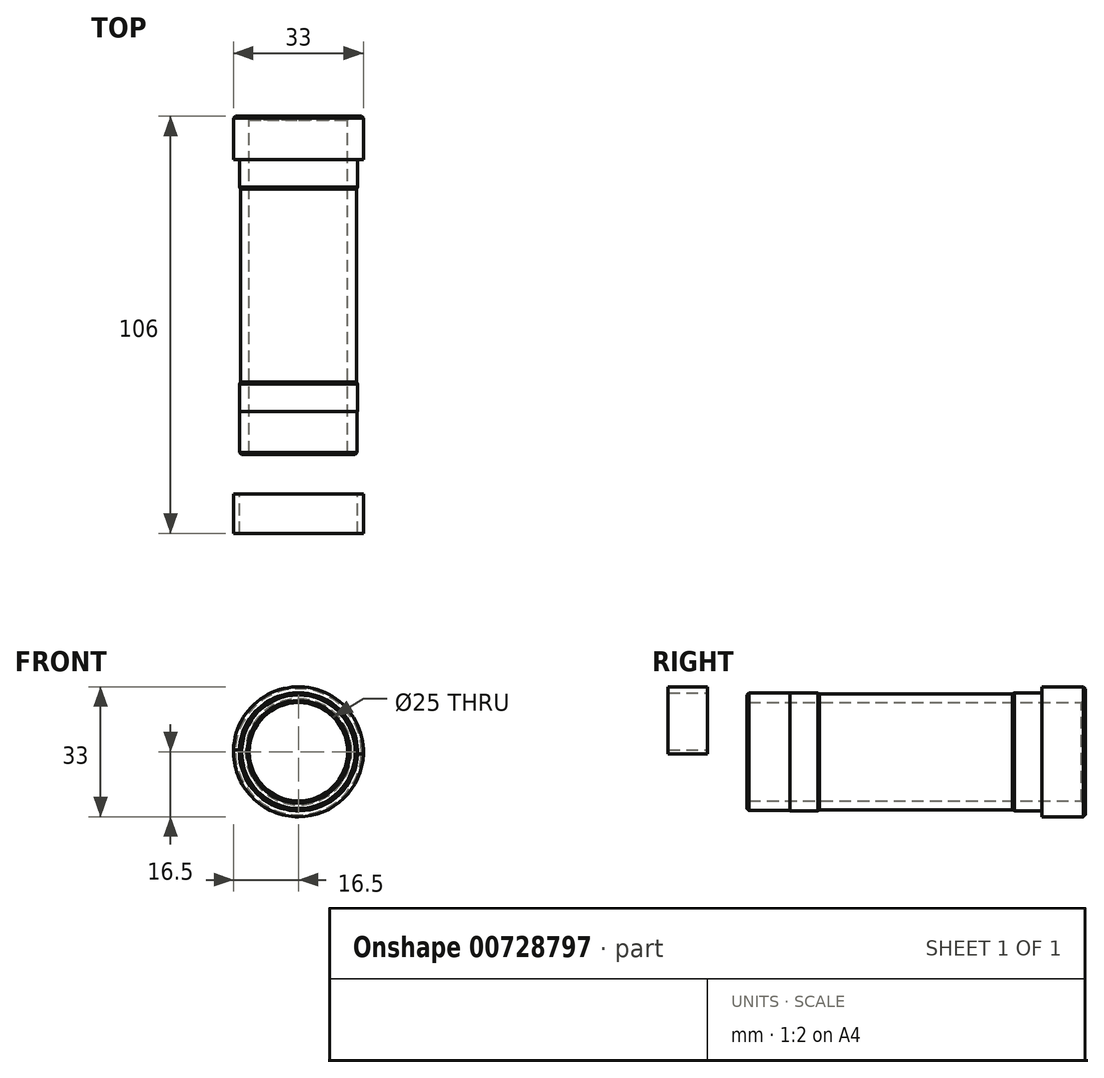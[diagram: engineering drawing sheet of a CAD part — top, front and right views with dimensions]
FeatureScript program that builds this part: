
annotation { "Feature Type Name" : "Feature", "Feature Type Description" : "" }
export const myFeature = defineFeature(function(context is Context, id is Id, definition is map)
    precondition{}
    {
        {
            var Q0;
            Q0=qCreatedBy(makeId("Front.planeOp"),FACE);
            var sketch = newSketch(context, id + "F0", { "sketchPlane" : qUnion([Q0])});
            skCircle(sketch, "E0", {"center": v(0, 0) * mm, "radius": 12.5 * mm});
            skCircle(sketch, "E1", {"center": v(0, 0) * mm, "radius": 16.5 * mm});
            skSolve(sketch);
        }
        {
            var Q0;
            Q0=makeQuery(id+"F0.imprint","IMPRINT",FACE,{"disambiguationData":[TD([[makeQuery(id+"F0.imprint","IMPRINT",EDGE,{"derivedFrom":sQuery(id+"F0.wireOp",EDGE,"E0")}),-1.0]])]});
            extrude(context, id + "F1", {"entities" : qUnion([Q0]), "depth" : 11 * mm, "offsetDistance" : 25 * mm});
        }
        {
            var Q0;
            Q0=makeQuery(id+"F1.opExtrude","CAP_FACE",FACE,{"disambiguationData":[OSD([sQuery(id+"F0.wireOp",EDGE,"E0"),sQuery(id+"F0.wireOp",EDGE,"E1")])],"isStart":false});
            var sketch = newSketch(context, id + "F2", { "sketchPlane" : qUnion([Q0])});
            skCircle(sketch, "E2", {"center": v(0, 0) * mm, "radius": 15 * mm});
            skSolve(sketch);
        }
        {
            var Q0;
            Q0=makeQuery(id+"F2.imprint","IMPRINT",FACE,{"disambiguationData":[TD([[makeQuery(id+"F2.imprint","IMPRINT",EDGE,{"derivedFrom":sQuery(id+"F2.wireOp",EDGE,"E2")}),1.0]])]});
            extrude(context, id + "F3", {"entities" : qUnion([Q0]), "operationType" : NewBodyOperationType.ADD, "depth" : 7.5 * mm, "offsetDistance" : 25 * mm});
        }
        {
            var Q0;
            Q0=makeQuery(id+"F3.opExtrude","CAP_FACE",FACE,{"disambiguationData":[OSD([sQuery(id+"F0.wireOp",EDGE,"E0"),sQuery(id+"F2.wireOp",EDGE,"E2")])],"isStart":false});
            var sketch = newSketch(context, id + "F4", { "sketchPlane" : qUnion([Q0])});
            skCircle(sketch, "E3", {"center": v(0, 0) * mm, "radius": 14.75 * mm});
            skSolve(sketch);
        }
        {
            var Q0;
            Q0=makeQuery(id+"F4.imprint","IMPRINT",FACE,{"disambiguationData":[TD([[makeQuery(id+"F4.imprint","IMPRINT",EDGE,{"derivedFrom":sQuery(id+"F4.wireOp",EDGE,"E3")}),1.0]])]});
            extrude(context, id + "F5", {"entities" : qUnion([Q0]), "operationType" : NewBodyOperationType.ADD, "depth" : 49 * mm, "offsetDistance" : 25 * mm});
        }
        {
            var Q0;
            Q0=makeQuery(id+"F5.opExtrude","CAP_FACE",FACE,{"disambiguationData":[OSD([sQuery(id+"F0.wireOp",EDGE,"E0"),sQuery(id+"F4.wireOp",EDGE,"E3")])],"isStart":false});
            var sketch = newSketch(context, id + "F6", { "sketchPlane" : qUnion([Q0])});
            skCircle(sketch, "E4", {"center": v(0, 0) * mm, "radius": 15 * mm});
            skSolve(sketch);
        }
        {
            var Q0;
            Q0=makeQuery(id+"F6.imprint","IMPRINT",FACE,{"disambiguationData":[TD([[makeQuery(id+"F6.imprint","IMPRINT",EDGE,{"derivedFrom":makeQuery(id+"F5.opExtrude","CAP_EDGE",EDGE,{"disambiguationData":[OSD([sQuery(id+"F4.wireOp",EDGE,"E3")])],"isStart":false})}),1.0]])]});
            var Q1;
            Q1=makeQuery(id+"F6.imprint","IMPRINT",FACE,{"disambiguationData":[TD([[makeQuery(id+"F6.imprint","IMPRINT",EDGE,{"derivedFrom":sQuery(id+"F6.wireOp",EDGE,"E4")}),1.0]])]});
            extrude(context, id + "F7", {"entities" : qUnion([Q0, Q1]), "operationType" : NewBodyOperationType.ADD, "depth" : 7.5 * mm, "offsetDistance" : 25 * mm});
        }
        {
            var Q0;
            Q0=makeQuery(id+"F7.opExtrude","CAP_FACE",FACE,{"disambiguationData":[OSD([sQuery(id+"F0.wireOp",EDGE,"E0"),sQuery(id+"F6.wireOp",EDGE,"E4")])],"isStart":false});
            var sketch = newSketch(context, id + "F8", { "sketchPlane" : qUnion([Q0])});
            skCircle(sketch, "E5", {"center": v(0, 0) * mm, "radius": 14.93 * mm});
            skSolve(sketch);
        }
        {
            var Q0;
            Q0=makeQuery(id+"F8.imprint","IMPRINT",FACE,{"disambiguationData":[TD([[makeQuery(id+"F8.imprint","IMPRINT",EDGE,{"derivedFrom":sQuery(id+"F8.wireOp",EDGE,"E5")}),1.0]])]});
            extrude(context, id + "F9", {"entities" : qUnion([Q0]), "operationType" : NewBodyOperationType.ADD, "depth" : 11 * mm, "offsetDistance" : 25 * mm});
        }
        {
            var Q0;
            Q0=makeQuery(id+"F1.opExtrude","CAP_EDGE",EDGE,{"disambiguationData":[OSD([sQuery(id+"F0.wireOp",EDGE,"E1")])],"isStart":true});
            chamfer(context, id + "F10", {"entities" : qUnion([Q0]), "width" : 0.5 * mm, "tangentPropagation" : true});
        }
        {
            var Q0;
            Q0=makeQuery(id+"F1.opExtrude","CAP_EDGE",EDGE,{"disambiguationData":[OSD([sQuery(id+"F0.wireOp",EDGE,"E0")])],"isStart":true});
            chamfer(context, id + "F11", {"entities" : qUnion([Q0]), "width" : 1 * mm, "tangentPropagation" : true});
        }
        {
            var Q0;
            Q0=makeQuery(id+"F3.opExtrude","CAP_EDGE",EDGE,{"disambiguationData":[OSD([sQuery(id+"F2.wireOp",EDGE,"E2")])],"isStart":false});
            chamfer(context, id + "F12", {"entities" : qUnion([Q0]), "chamferType" : ChamferType.TWO_OFFSETS, "width1" : 0.25 * mm, "oppositeDirection" : false, "width2" : 0.5 * mm, "tangentPropagation" : true});
        }
        {
            var Q0;
            Q0=makeQuery(id+"F7.opExtrude","CAP_EDGE",EDGE,{"disambiguationData":[OSD([sQuery(id+"F6.wireOp",EDGE,"E4")])],"isStart":true});
            chamfer(context, id + "F13", {"entities" : qUnion([Q0]), "chamferType" : ChamferType.TWO_OFFSETS, "width1" : 0.5 * mm, "oppositeDirection" : false, "width2" : 0.25 * mm, "tangentPropagation" : true});
        }
        {
            var Q0;
            Q0=makeQuery(id+"F9.opExtrude","CAP_EDGE",EDGE,{"disambiguationData":[OSD([sQuery(id+"F8.wireOp",EDGE,"E5")])],"isStart":false});
            var Q1;
            Q1=makeQuery(id+"F9.opExtrude","CAP_EDGE",EDGE,{"disambiguationData":[OSD([sQuery(id+"F0.wireOp",EDGE,"E0")])],"isStart":false});
            chamfer(context, id + "F14", {"entities" : qUnion([Q0, Q1]), "width" : 0.5 * mm, "tangentPropagation" : true});
        }
        {
            var Q0;
            Q0=makeQuery(id+"F9.opExtrude","CAP_FACE",FACE,{"disambiguationData":[OSD([sQuery(id+"F0.wireOp",EDGE,"E0"),sQuery(id+"F8.wireOp",EDGE,"E5")])],"isStart":false});
            var sketch = newSketch(context, id + "F15", { "sketchPlane" : qUnion([Q0])});
            skCircle(sketch, "E6", {"center": v(0, 0) * mm, "radius": 15 * mm});
            skCircle(sketch, "E7", {"center": v(0, 0) * mm, "radius": 16.5 * mm});
            skLineSegment(sketch, "E8.bottom", {"start": v(20, 0.5) * mm, "end": v(-20, 0.5) * mm});
            skLineSegment(sketch, "E8.top", {"start": v(20, -0.5) * mm, "end": v(-20, -0.5) * mm});
            skLineSegment(sketch, "E8.left", {"start": v(20, 0.5) * mm, "end": v(20, -0.5) * mm});
            skLineSegment(sketch, "E8.right", {"start": v(-20, 0.5) * mm, "end": v(-20, -0.5) * mm});
            skSolve(sketch);
        }
        {
            var Q0;
            {var subQ0=sQuery(id+"F15.wireOp",EDGE,"E8.bottom");var subQ1=sQuery(id+"F15.wireOp",EDGE,"E6");var subQ2=makeQuery(id+"F15.imprint","INTERSECT",VERTEX,{"disambiguationData":[OD(0.0)],"derivedFrom":[subQ1,subQ0]});Q0=makeQuery(id+"F15.imprint","IMPRINT",FACE,{"disambiguationData":[TD([[makeQuery(id+"F15.imprint","IMPRINT",EDGE,{"disambiguationData":[TD([[subQ2,1.0]])],"derivedFrom":subQ1}),-1.0]])]});}
            var Q1;
            {var subQ0=sQuery(id+"F15.wireOp",EDGE,"E8.top");var subQ1=sQuery(id+"F15.wireOp",EDGE,"E6");var subQ2=makeQuery(id+"F15.imprint","INTERSECT",VERTEX,{"disambiguationData":[OD(0.0)],"derivedFrom":[subQ1,subQ0]});Q1=makeQuery(id+"F15.imprint","IMPRINT",FACE,{"disambiguationData":[TD([[makeQuery(id+"F15.imprint","IMPRINT",EDGE,{"disambiguationData":[TD([[subQ2,-1.0]])],"derivedFrom":subQ1}),-1.0]])]});}
            var Q2;
            {var subQ0=sQuery(id+"F15.wireOp",EDGE,"E8.bottom");var subQ1=sQuery(id+"F15.wireOp",EDGE,"E6");var subQ2=makeQuery(id+"F15.imprint","INTERSECT",VERTEX,{"disambiguationData":[OD(0.0)],"derivedFrom":[subQ1,subQ0]});Q2=makeQuery(id+"F15.imprint","IMPRINT",FACE,{"disambiguationData":[TD([[makeQuery(id+"F15.imprint","IMPRINT",EDGE,{"disambiguationData":[TD([[subQ2,-1.0]])],"derivedFrom":subQ1}),-1.0]])]});}
            extrude(context, id + "F16", {"entities" : qUnion([Q0, Q1, Q2]), "depth" : 10 * mm, "offsetDistance" : 25 * mm});
        }
        {
            var Q0;
            Q0=makeQuery(id+"F16.opExtrude","SWEPT_BODY",BODY,{"disambiguationData":[OSD([sQuery(id+"F15.wireOp",EDGE,"E6"),sQuery(id+"F15.wireOp",EDGE,"E7"),sQuery(id+"F15.wireOp",EDGE,"E8.bottom"),sQuery(id+"F15.wireOp",EDGE,"E8.top")])]});
            transform(context, id + "F17", {"entities" : qUnion([Q0]), "transformType" : TransformType.TRANSLATION_3D, "dx" : 0 * mm, "dy" : -10 * mm, "dz" : 0 * mm, "makeCopy" : false});
        }
    });
